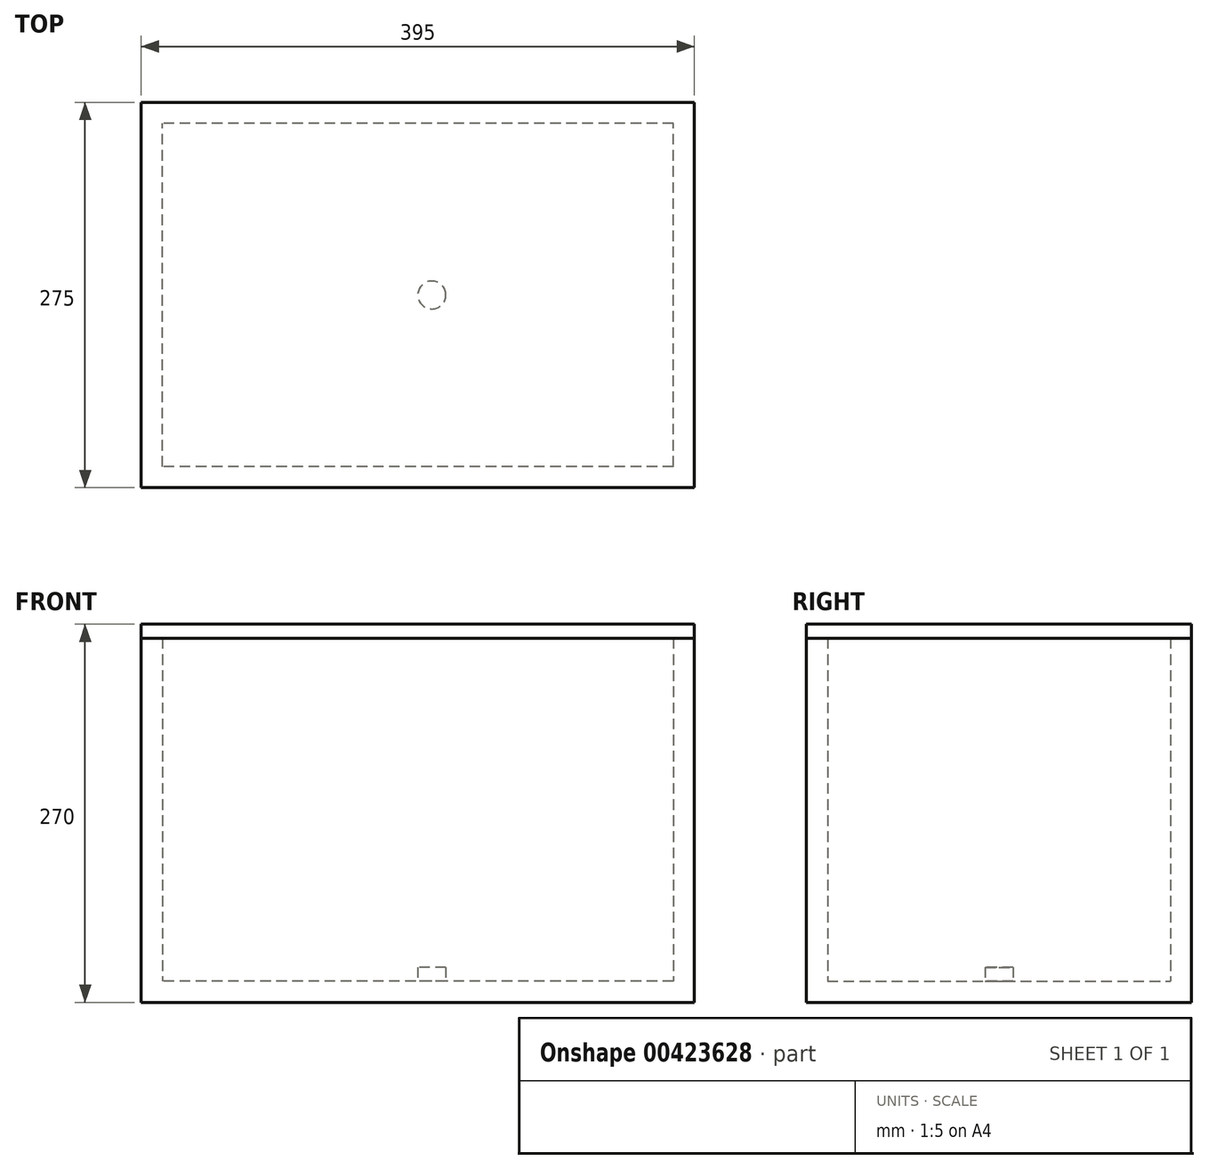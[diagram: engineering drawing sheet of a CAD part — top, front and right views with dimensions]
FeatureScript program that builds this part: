
annotation { "Feature Type Name" : "Feature", "Feature Type Description" : "" }
export const myFeature = defineFeature(function(context is Context, id is Id, definition is map)
    precondition{}
    {
        {
            var Q0;
            Q0=qCreatedBy(makeId("Top.planeOp"),FACE);
            var sketch = newSketch(context, id + "F0", { "sketchPlane" : qUnion([Q0])});
            skLineSegment(sketch, "E0.bottom", {"start": v(197.5, -137.5) * mm, "end": v(-197.5, -137.5) * mm});
            skLineSegment(sketch, "E0.top", {"start": v(197.5, 137.5) * mm, "end": v(-197.5, 137.5) * mm});
            skLineSegment(sketch, "E0.left", {"start": v(197.5, -137.5) * mm, "end": v(197.5, 137.5) * mm});
            skLineSegment(sketch, "E0.right", {"start": v(-197.5, -137.5) * mm, "end": v(-197.5, 137.5) * mm});
            skPoint(sketch, "E0.middle", {"position": v(0, 0) * mm});
            skSolve(sketch);
        }
        {
            var Q0;
            Q0=makeQuery(id+"F0.imprint","IMPRINT",FACE,{"disambiguationData":[TD([[makeQuery(id+"F0.imprint","IMPRINT",EDGE,{"derivedFrom":sQuery(id+"F0.wireOp",EDGE,"E0.bottom")}),-1.0]])]});
            extrude(context, id + "F1", {"entities" : qUnion([Q0]), "depth" : 260 * mm});
        }
        {
            var Q0;
            Q0=makeQuery(id+"F1.opExtrude","CAP_FACE",FACE,{"disambiguationData":[OSD([sQuery(id+"F0.wireOp",EDGE,"E0.bottom"),sQuery(id+"F0.wireOp",EDGE,"E0.top"),sQuery(id+"F0.wireOp",EDGE,"E0.left"),sQuery(id+"F0.wireOp",EDGE,"E0.right")])],"isStart":false});
            shell(context, id + "F2", {"entities" : qUnion([Q0]), "thickness" : 15 * mm});
        }
        {
            var Q0;
            Q0=makeQuery(id+"F1.opExtrude","CAP_FACE",FACE,{"disambiguationData":[OSD([sQuery(id+"F0.wireOp",EDGE,"E0.bottom"),sQuery(id+"F0.wireOp",EDGE,"E0.top"),sQuery(id+"F0.wireOp",EDGE,"E0.left"),sQuery(id+"F0.wireOp",EDGE,"E0.right")])],"isStart":false});
            var sketch = newSketch(context, id + "F3", { "sketchPlane" : qUnion([Q0])});
            skLineSegment(sketch, "E1.0", {"start": v(-197.5, -137.5) * mm, "end": v(-197.5, 137.5) * mm});
            skLineSegment(sketch, "E2.0", {"start": v(197.5, -137.5) * mm, "end": v(-197.5, -137.5) * mm});
            skLineSegment(sketch, "E3.0", {"start": v(197.5, 137.5) * mm, "end": v(-197.5, 137.5) * mm});
            skLineSegment(sketch, "E4.0", {"start": v(197.5, -137.5) * mm, "end": v(197.5, 137.5) * mm});
            skSolve(sketch);
        }
        {
            var Q0;
            {var subQ0=sQuery(id+"F0.wireOp",EDGE,"E0.bottom");Q0=makeQuery(id+"F3.imprint","IMPRINT",FACE,{"disambiguationData":[TD([[makeQuery(id+"F3.imprint","IMPRINT",EDGE,{"derivedFrom":makeQuery(id+"F2.opShell","OFFSET_EDGE",EDGE,{"disambiguationData":[OSD([subQ0]),TDD([makeQuery(id+"F1.opExtrude","CAP_EDGE",EDGE,{"disambiguationData":[OSD([subQ0])],"isStart":false})])]})}),-1.0]])]});}
            var Q1;
            Q1=makeQuery(id+"F3.imprint","IMPRINT",FACE,{"disambiguationData":[TD([[makeQuery(id+"F3.imprint","IMPRINT",EDGE,{"derivedFrom":sQuery(id+"F3.wireOp",EDGE,"E1.0")}),-1.0]])]});
            extrude(context, id + "F4", {"entities" : qUnion([Q0, Q1]), "depth" : 10 * mm});
        }
        {
            var Q0;
            Q0=makeQuery(id+"F2.opShell","OFFSET_FACE",FACE,{"disambiguationData":[OSD([sQuery(id+"F0.wireOp",EDGE,"E0.bottom"),sQuery(id+"F0.wireOp",EDGE,"E0.top"),sQuery(id+"F0.wireOp",EDGE,"E0.left"),sQuery(id+"F0.wireOp",EDGE,"E0.right")])]});
            var sketch = newSketch(context, id + "F5", { "sketchPlane" : qUnion([Q0])});
            skCircle(sketch, "E5", {"center": v(10, 0) * mm, "radius": 10 * mm});
            skSolve(sketch);
        }
        {
            var Q0;
            Q0=makeQuery(id+"F5.imprint","IMPRINT",FACE,{"disambiguationData":[TD([[makeQuery(id+"F5.imprint","IMPRINT",EDGE,{"derivedFrom":sQuery(id+"F5.wireOp",EDGE,"E5")}),1.0]])]});
            extrude(context, id + "F6", {"entities" : qUnion([Q0]), "operationType" : NewBodyOperationType.ADD, "depth" : 10 * mm});
        }
    });
